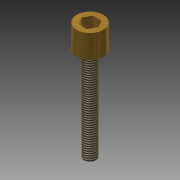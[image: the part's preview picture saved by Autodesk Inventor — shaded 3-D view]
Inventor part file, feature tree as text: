
AUTODESK INVENTOR PART (.ipt)
format: ipt  version: 2015 (Build 190159000, 159)  size: 99,328 bytes
history: native  units: mm
features: extrude x3, sketch x3, thread x1, chamfer x1
ambient origin geometry x8: Origin, YZ Plane, XZ Plane, XY Plane, X Axis, Y Axis, Z Axis, Center Point
bodies: 实体1 (feature_tree)
feature tree (8):
  extrude  "拉伸1"  Depth=8.0mm TaperAngle=0.0deg
  extrude  "拉伸2"  Depth=32.0mm TaperAngle=0.0deg
  thread  "螺纹1"  [1 undecoded]
  chamfer  "倒角1"  Distance=2.0mm Angle=45.0deg
  extrude  "拉伸3"  Depth=5.0mm
  sketch  "草图1"  dims[d0=9.0mm d1=8.0mm d2=0.0mm]
  sketch  "草图2"  dims[d3=4.0mm d4=32.0mm d5=0.0mm d6=10.0mm d7=0.0mm d8=0.25mm d9=2.0mm d10=45.0deg]
  sketch  "草图3"  dims[d11=0.652407mm d12=5.0mm d13=5.0mm d14=0.0mm]
note: 1 required parameter value undecoded (feature->parameter linkage not recoverable at this tier; creation-order binding heuristic only, values carry confidence <= 0.55)
